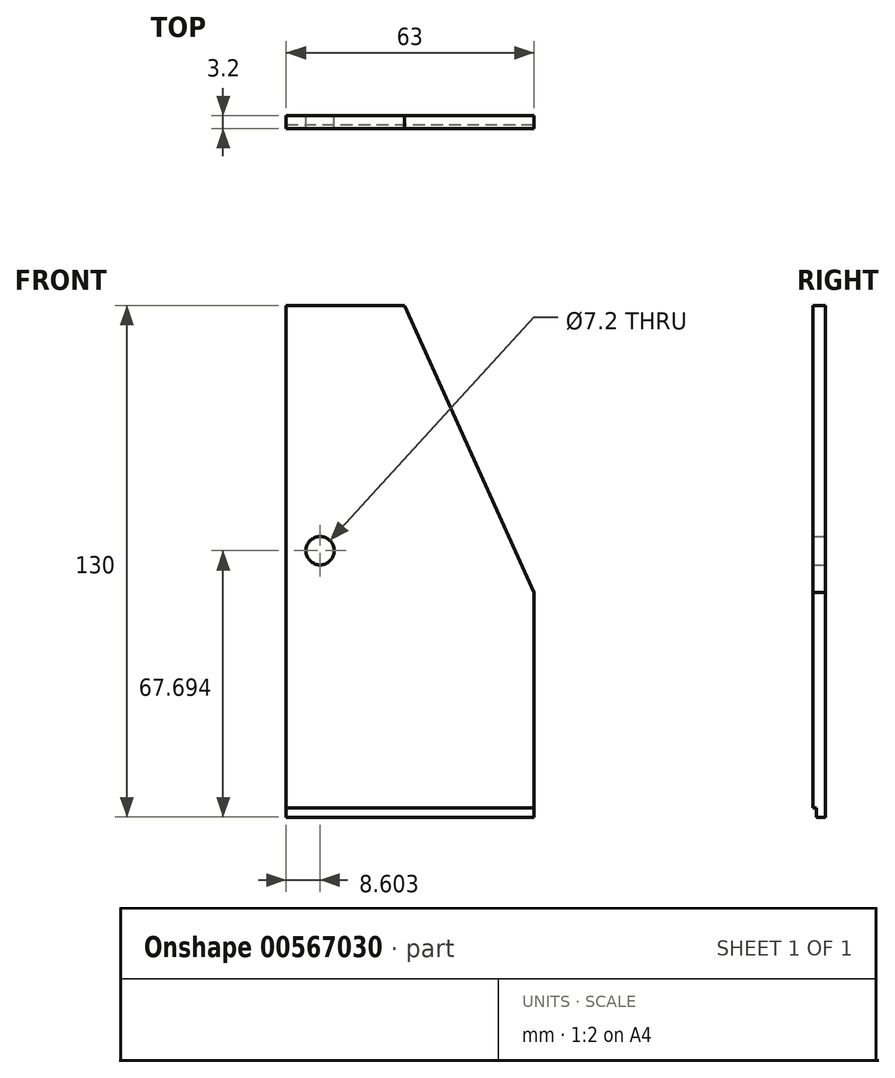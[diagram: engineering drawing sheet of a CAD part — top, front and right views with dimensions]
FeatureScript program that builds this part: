
annotation { "Feature Type Name" : "Feature", "Feature Type Description" : "" }
export const myFeature = defineFeature(function(context is Context, id is Id, definition is map)
    precondition{}
    {
        {
            var Q0;
            Q0=qCreatedBy(makeId("Front.planeOp"),FACE);
            var sketch = newSketch(context, id + "F0", { "sketchPlane" : qUnion([Q0])});
            skLineSegment(sketch, "E0.bottom", {"start": v(-43.62, 4.44) * mm, "end": v(19.38, 4.44) * mm});
            skLineSegment(sketch, "E0.top", {"start": v(-43.62, -52.68) * mm, "end": v(19.38, -52.68) * mm});
            skLineSegment(sketch, "E0.left", {"start": v(-43.62, 4.44) * mm, "end": v(-43.62, -52.68) * mm});
            skLineSegment(sketch, "E0.right", {"start": v(19.38, 4.44) * mm, "end": v(19.38, -52.68) * mm});
            skLineSegment(sketch, "E1.bottom", {"start": v(-43.62, 77.32) * mm, "end": v(-13.62, 77.32) * mm});
            skLineSegment(sketch, "E1.top", {"start": v(-43.62, 31.44) * mm, "end": v(-13.62, 31.44) * mm});
            skLineSegment(sketch, "E1.left", {"start": v(-43.62, 77.32) * mm, "end": v(-43.62, 31.44) * mm});
            skLineSegment(sketch, "E1.right", {"start": v(-13.62, 77.32) * mm, "end": v(-13.62, 31.44) * mm});
            skLineSegment(sketch, "E2", {"start": v(-43.62, 77.32) * mm, "end": v(-43.62, -52.68) * mm});
            skLineSegment(sketch, "E3", {"start": v(-13.62, 77.32) * mm, "end": v(19.38, 4.44) * mm});
            skCircle(sketch, "E4", {"center": v(-35.02, 15.01) * mm, "radius": 3.6 * mm});
            skLineSegment(sketch, "E5", {"start": v(-43.62, -50.38) * mm, "end": v(19.38, -50.38) * mm});
            skSolve(sketch);
        }
        {
            var Q0;
            {var subQ1=sQuery(id+"F0.wireOp",EDGE,"E0.bottom");Q0=makeQuery(id+"F0.imprint","IMPRINT",FACE,{"disambiguationData":[TD([[makeQuery(id+"F0.imprint","IMPRINT",EDGE,{"derivedFrom":subQ1}),1.0]])]});}
            var Q1;
            {var subQ0=sQuery(id+"F0.wireOp",EDGE,"E1.bottom");Q1=makeQuery(id+"F0.imprint","IMPRINT",FACE,{"disambiguationData":[TD([[makeQuery(id+"F0.imprint","IMPRINT",EDGE,{"derivedFrom":subQ0}),-1.0]])]});}
            var Q2;
            {var subQ0=sQuery(id+"F0.wireOp",EDGE,"E0.bottom");Q2=makeQuery(id+"F0.imprint","IMPRINT",FACE,{"disambiguationData":[TD([[makeQuery(id+"F0.imprint","IMPRINT",EDGE,{"derivedFrom":subQ0}),-1.0]])]});}
            extrude(context, id + "F1", {"entities" : qUnion([Q0, Q1, Q2]), "depth" : 3.2 * mm, "offsetDistance" : 25 * mm});
        }
        {
            var Q0;
            Q0=qSketchRegion(id+"F0",true);
            extrude(context, id + "F2", {"entities" : qUnion([Q0]), "operationType" : NewBodyOperationType.ADD, "depth" : 2.3 * mm, "offsetDistance" : 25 * mm});
        }
    });
